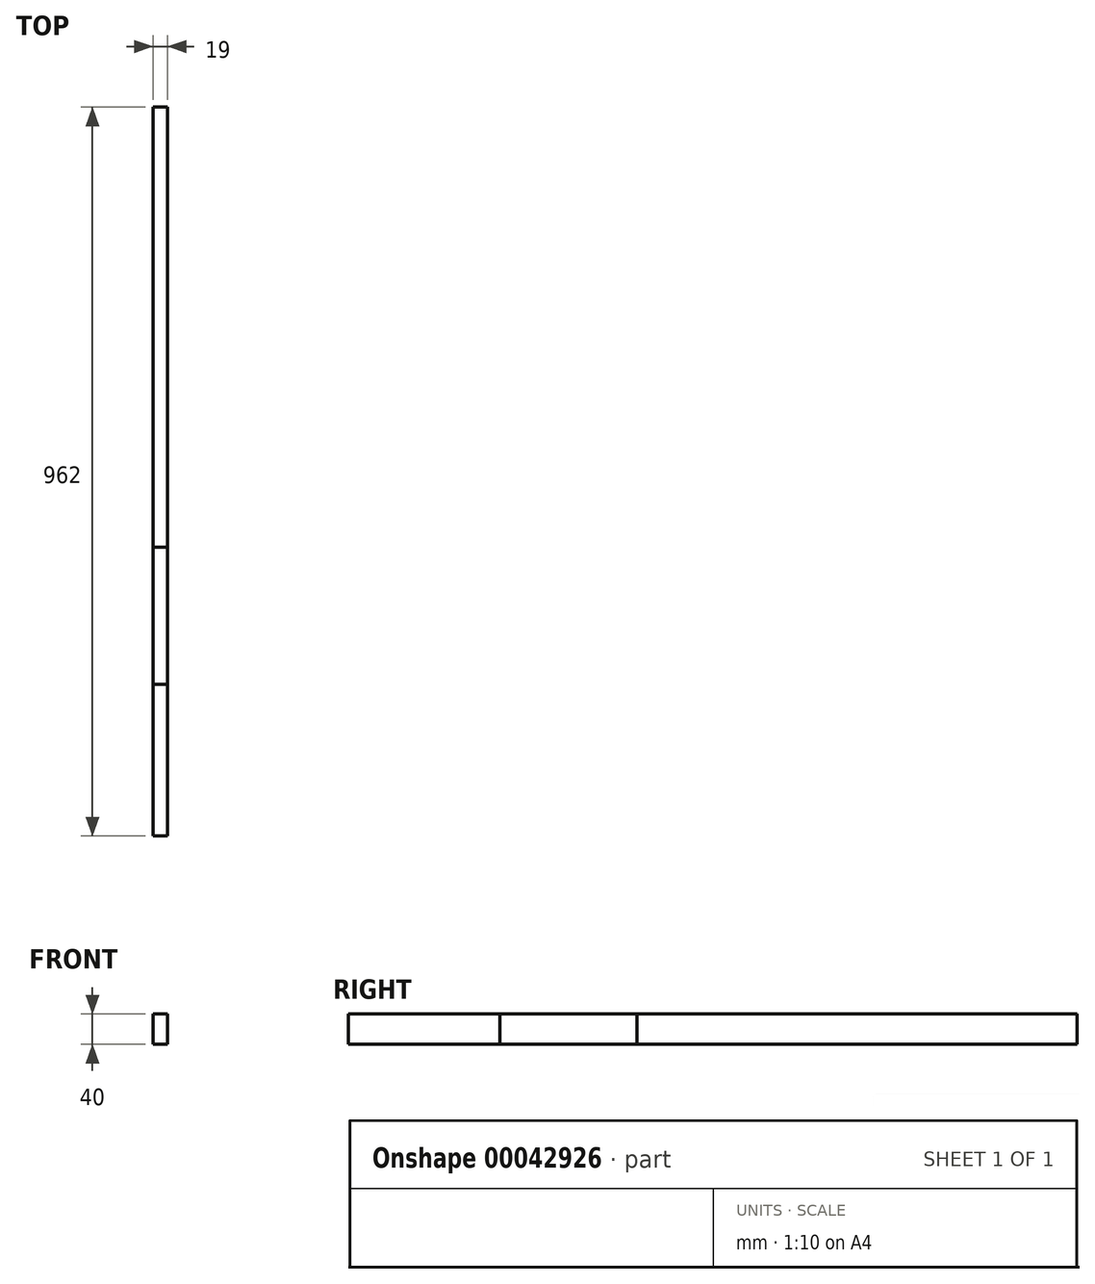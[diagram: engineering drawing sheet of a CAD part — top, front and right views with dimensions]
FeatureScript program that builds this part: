
annotation { "Feature Type Name" : "Feature", "Feature Type Description" : "" }
export const myFeature = defineFeature(function(context is Context, id is Id, definition is map)
    precondition{}
    {
        {
            assignVariable(context, id + "F0", {"name" : "CupboardThickness", "anyValue" : 19});
        }
        {
            var Q0;
            Q0=qCreatedBy(makeId("Front.planeOp"),FACE);
            var sketch = newSketch(context, id + "F1", { "sketchPlane" : qUnion([Q0])});
            skLineSegment(sketch, "E0.bottom", {"start": v(0, 0) * mm, "end": v(19, 0) * mm});
            skLineSegment(sketch, "E0.top", {"start": v(0, 40) * mm, "end": v(19, 40) * mm});
            skLineSegment(sketch, "E0.left", {"start": v(0, 0) * mm, "end": v(0, 40) * mm});
            skLineSegment(sketch, "E0.right", {"start": v(19, 0) * mm, "end": v(19, 40) * mm});
            skSolve(sketch);
        }
        {
            var Q0;
            Q0=makeQuery(id+"F1.imprint","IMPRINT",FACE,{"disambiguationData":[TD([[makeQuery(id+"F1.imprint","IMPRINT",EDGE,{"derivedFrom":sQuery(id+"F1.wireOp",EDGE,"E0.bottom")}),1.0]])]});
            extrude(context, id + "F2", {"entities" : qUnion([Q0]), "depth" : (800 - 2 * getVariable(context, 'CupboardThickness')) * mm});
        }
        {
            var Q0;
            Q0 = qSketchRegion(id + "F1", true);
            extrude(context, id + "F3", {"entities" : qUnion([Q0]), "depth" : ((1200 - 2 * getVariable(context, 'CupboardThickness')) / 2) * mm});
        }
        {
            var Q0;
            Q0 = qSketchRegion(id + "F1", true);
            extrude(context, id + "F4", {"entities" : qUnion([Q0]), "depth" : (1000 - 2 * getVariable(context, 'CupboardThickness')) * mm});
        }
    });
